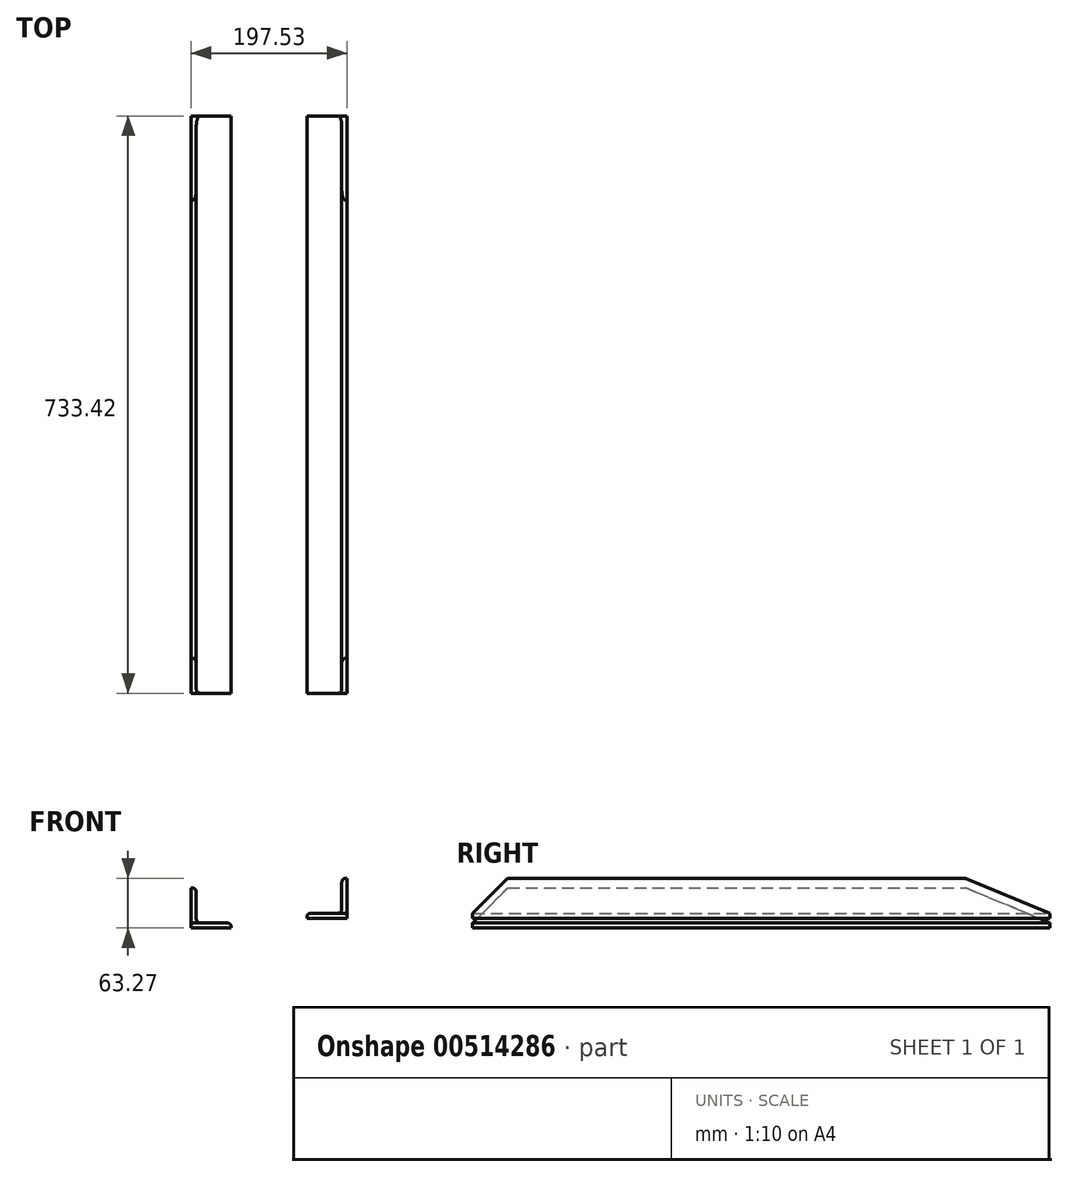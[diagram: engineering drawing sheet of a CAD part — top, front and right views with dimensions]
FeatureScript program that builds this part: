
annotation { "Feature Type Name" : "Feature", "Feature Type Description" : "" }
export const myFeature = defineFeature(function(context is Context, id is Id, definition is map)
    precondition{}
    {
        {
            var Q0;
            Q0=qCreatedBy(makeId("Front.planeOp"),FACE);
            var sketch = newSketch(context, id + "F0", { "sketchPlane" : qUnion([Q0])});
            skLineSegment(sketch, "E0.bottom", {"start": v(-74.04, -22.46) * mm, "end": v(-124.84, -22.46) * mm});
            skLineSegment(sketch, "E0.top", {"start": v(-118.5, 28.34) * mm, "end": v(-124.84, 28.34) * mm});
            skLineSegment(sketch, "E0.left", {"start": v(-74.04, -22.46) * mm, "end": v(-74.04, -16.11) * mm});
            skLineSegment(sketch, "E0.right", {"start": v(-124.84, -22.46) * mm, "end": v(-124.84, 28.34) * mm});
            skPoint(sketch, "E0.middle", {"position": v(-99.44, 2.94) * mm});
            skLineSegment(sketch, "E1.bottom", {"start": v(72.7, -9.99) * mm, "end": v(21.9, -9.99) * mm});
            skLineSegment(sketch, "E1.top", {"start": v(72.7, 40.81) * mm, "end": v(66.34, 40.81) * mm});
            skLineSegment(sketch, "E1.left", {"start": v(72.7, -9.99) * mm, "end": v(72.7, 40.81) * mm});
            skLineSegment(sketch, "E1.right", {"start": v(21.9, -9.99) * mm, "end": v(21.9, -3.64) * mm});
            skPoint(sketch, "E1.middle", {"position": v(47.3, 15.41) * mm});
            skLineSegment(sketch, "E2.0", {"start": v(-118.5, -16.11) * mm, "end": v(-118.5, 28.34) * mm});
            skLineSegment(sketch, "E3.0", {"start": v(-74.04, -16.11) * mm, "end": v(-118.5, -16.11) * mm});
            skLineSegment(sketch, "E4.0", {"start": v(66.34, -3.64) * mm, "end": v(21.9, -3.64) * mm});
            skLineSegment(sketch, "E5.0", {"start": v(66.34, -3.64) * mm, "end": v(66.34, 40.81) * mm});
            skPoint(sketch, "E6.orphan", {"position": v(-74.04, 28.34) * mm});
            skPoint(sketch, "E7.orphan", {"position": v(21.9, 40.81) * mm});
            skSolve(sketch);
        }
        {
            var Q0;
            Q0 = qSketchRegion(id + "F0", true);
            extrude(context, id + "F1", {"entities" : qUnion([Q0]), "endBound" : BoundingType.SYMMETRIC, "depth" : 733.42 * mm});
        }
        {
            var Q0;
            Q0=makeQuery(id+"F1.opExtrude","SWEPT_EDGE",EDGE,{"disambiguationData":[OSD([sQuery(id+"F0.wireOp",EDGE,"E0.top"),sQuery(id+"F0.wireOp",EDGE,"E2.0")])]});
            var Q1;
            Q1=makeQuery(id+"F1.opExtrude","SWEPT_EDGE",EDGE,{"disambiguationData":[OSD([sQuery(id+"F0.wireOp",EDGE,"E2.0"),sQuery(id+"F0.wireOp",EDGE,"E3.0")])]});
            var Q2;
            Q2=makeQuery(id+"F1.opExtrude","SWEPT_EDGE",EDGE,{"disambiguationData":[OSD([sQuery(id+"F0.wireOp",EDGE,"E0.left"),sQuery(id+"F0.wireOp",EDGE,"E3.0")])]});
            var Q3;
            Q3=makeQuery(id+"F1.opExtrude","SWEPT_EDGE",EDGE,{"disambiguationData":[OSD([sQuery(id+"F0.wireOp",EDGE,"E1.right"),sQuery(id+"F0.wireOp",EDGE,"E4.0")])]});
            var Q4;
            Q4=makeQuery(id+"F1.opExtrude","SWEPT_EDGE",EDGE,{"disambiguationData":[OSD([sQuery(id+"F0.wireOp",EDGE,"E4.0"),sQuery(id+"F0.wireOp",EDGE,"E5.0")])]});
            var Q5;
            Q5=makeQuery(id+"F1.opExtrude","SWEPT_EDGE",EDGE,{"disambiguationData":[OSD([sQuery(id+"F0.wireOp",EDGE,"E1.top"),sQuery(id+"F0.wireOp",EDGE,"E5.0")])]});
            fillet(context, id + "F2", {"entities" : qUnion([Q0, Q1, Q2, Q3, Q4, Q5]), "radius" : 5.08 * mm, "tangentPropagation" : true, "allowEdgeOverflow" : false});
        }
        {
            var Q0;
            Q0=makeQuery(id+"F1.opExtrude","SWEPT_FACE",FACE,{"disambiguationData":[OSD([sQuery(id+"F0.wireOp",EDGE,"E0.right")])]});
            var sketch = newSketch(context, id + "F3", { "sketchPlane" : qUnion([Q0])});
            skPoint(sketch, "E8.0", {"position": v(366.71, -16.11) * mm});
            skLineSegment(sketch, "E9", {"start": v(366.71, -16.11) * mm, "end": v(366.71, 28.34) * mm});
            skLineSegment(sketch, "E10", {"start": v(366.71, -16.11) * mm, "end": v(283.4, 67.2) * mm});
            skPoint(sketch, "E11.0", {"position": v(-366.71, -16.11) * mm});
            skLineSegment(sketch, "E12", {"start": v(-366.71, -16.11) * mm, "end": v(-366.71, 28.34) * mm});
            skLineSegment(sketch, "E13", {"start": v(-366.71, -16.11) * mm, "end": v(-263.6, 26.6) * mm});
            skLineSegment(sketch, "E14", {"start": v(-366.71, -16.11) * mm, "end": v(-251.96, 31.42) * mm});
            skSolve(sketch);
        }
        {
            var Q0;
            Q0 = qSketchRegion(id + "F3", true);
            var Q1;
            {var subQ0=sQuery(id+"F3.wireOp",EDGE,"E12");Q1=makeQuery(id+"F3.imprint","IMPRINT",FACE,{"disambiguationData":[TD([[makeQuery(id+"F3.imprint","IMPRINT",EDGE,{"derivedFrom":subQ0}),-1.0]])]});}
            var Q2;
            {var subQ0=sQuery(id+"F3.wireOp",EDGE,"E9");Q2=makeQuery(id+"F3.imprint","IMPRINT",FACE,{"disambiguationData":[TD([[makeQuery(id+"F3.imprint","IMPRINT",EDGE,{"derivedFrom":subQ0}),1.0]])]});}
            extrude(context, id + "F4", {"entities" : qUnion([Q0, Q1, Q2]), "operationType" : NewBodyOperationType.REMOVE, "oppositeDirection" : true, "depth" : 25.4 * mm});
        }
        {
            var Q0;
            Q0=makeQuery(id+"F1.opExtrude","SWEPT_FACE",FACE,{"disambiguationData":[OSD([sQuery(id+"F0.wireOp",EDGE,"E1.left")])]});
            var sketch = newSketch(context, id + "F5", { "sketchPlane" : qUnion([Q0])});
            skPoint(sketch, "E15.0", {"position": v(-366.71, -3.64) * mm});
            skPoint(sketch, "E16.0", {"position": v(366.71, -3.64) * mm});
            skLineSegment(sketch, "E17", {"start": v(366.71, -3.64) * mm, "end": v(247.68, -3.64) * mm});
            skLineSegment(sketch, "E18", {"start": v(366.71, -3.64) * mm, "end": v(212.58, 60.2) * mm});
            skLineSegment(sketch, "E19", {"start": v(-366.71, -3.64) * mm, "end": v(-366.71, 40.81) * mm});
            skLineSegment(sketch, "E20", {"start": v(-366.71, -3.64) * mm, "end": v(-261.85, 101.23) * mm});
            skSolve(sketch);
        }
        {
            var Q0;
            Q0 = qSketchRegion(id + "F5", true);
            var Q1;
            {var subQ0=sQuery(id+"F5.wireOp",EDGE,"E18");var subQ1=sQuery(id+"F0.wireOp",EDGE,"E1.left");var subQ2=makeQuery(id+"F1.opExtrude","CAP_EDGE",EDGE,{"disambiguationData":[OSD([subQ1])],"isStart":true});var subQ3=makeQuery(id+"F5.imprint","INTERSECT",VERTEX,{"derivedFrom":[subQ2,subQ0]});Q1=makeQuery(id+"F5.imprint","IMPRINT",FACE,{"disambiguationData":[TD([[makeQuery(id+"F5.imprint","IMPRINT",EDGE,{"disambiguationData":[TD([[subQ3,-1.0]])],"derivedFrom":subQ0}),-1.0]])]});}
            var Q2;
            {var subQ0=sQuery(id+"F5.wireOp",EDGE,"E19");Q2=makeQuery(id+"F5.imprint","IMPRINT",FACE,{"disambiguationData":[TD([[makeQuery(id+"F5.imprint","IMPRINT",EDGE,{"derivedFrom":subQ0}),-1.0]])]});}
            extrude(context, id + "F6", {"entities" : qUnion([Q0, Q1, Q2]), "operationType" : NewBodyOperationType.REMOVE, "oppositeDirection" : true, "depth" : 25.4 * mm});
        }
    });
